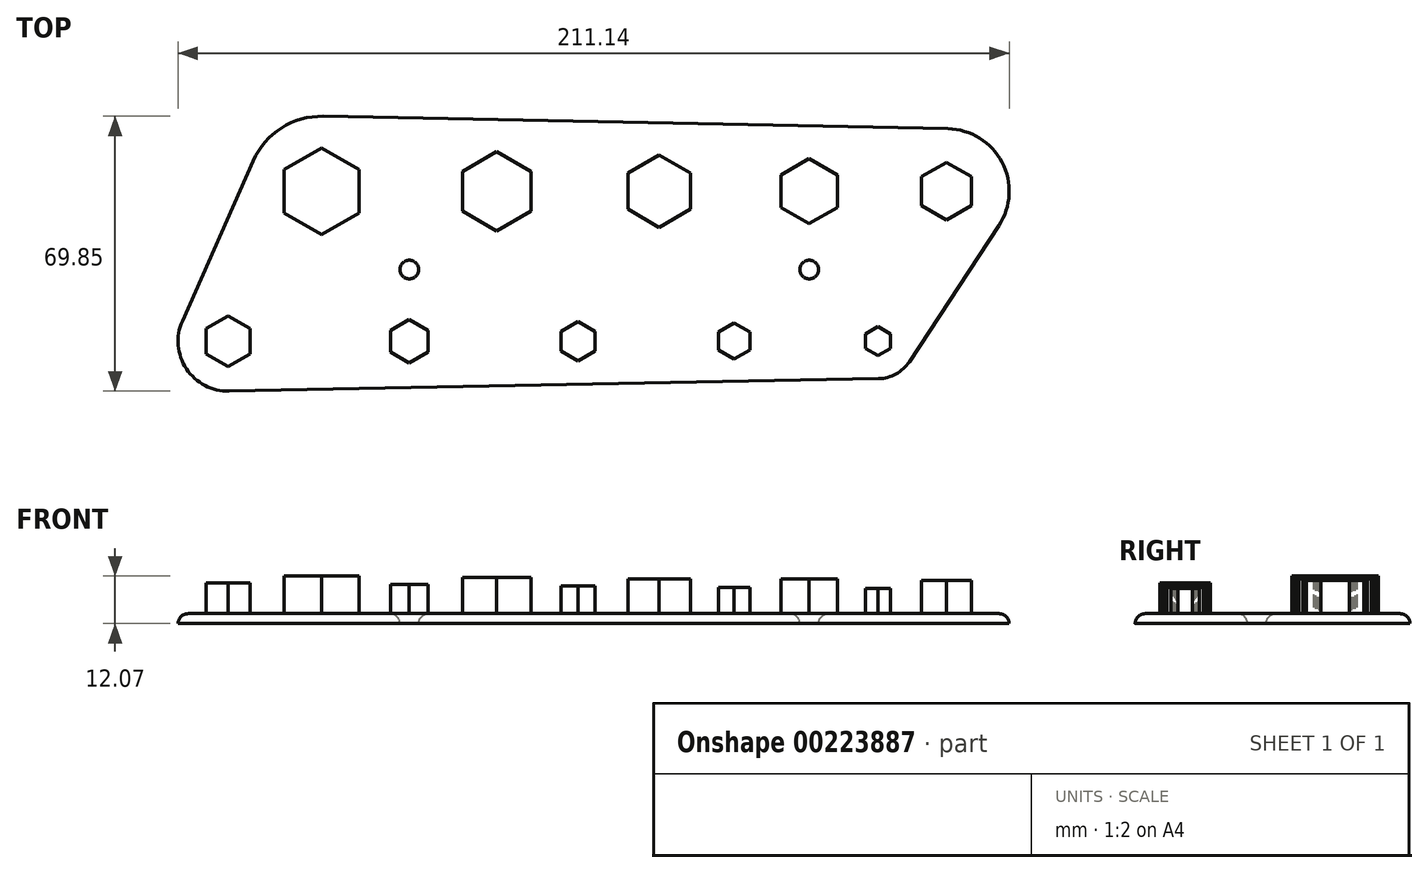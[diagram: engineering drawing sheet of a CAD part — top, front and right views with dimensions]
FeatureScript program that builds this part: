
annotation { "Feature Type Name" : "Feature", "Feature Type Description" : "" }
export const myFeature = defineFeature(function(context is Context, id is Id, definition is map)
    precondition{}
    {
        {
            var Q0;
            Q0=qCreatedBy(makeId("Top.planeOp"),FACE);
            var sketch = newSketch(context, id + "F0", { "sketchPlane" : qUnion([Q0])});
            skLineSegment(sketch, "E0", {"start": v(0, 0) * mm, "end": v(44.45, 0) * mm});
            skLineSegment(sketch, "E1", {"start": v(85.73, 0) * mm, "end": v(123.83, 0) * mm});
            skLineSegment(sketch, "E2", {"start": v(85.73, 0) * mm, "end": v(44.45, 0) * mm});
            skLineSegment(sketch, "E3", {"start": v(123.83, 0) * mm, "end": v(158.75, 0) * mm});
            skLineSegment(sketch, "E4", {"start": v(22.23, 0) * mm, "end": v(22.23, -38.1) * mm});
            skLineSegment(sketch, "E5", {"start": v(65.09, 0) * mm, "end": v(65.09, -38.1) * mm});
            skLineSegment(sketch, "E6", {"start": v(104.78, -38.1) * mm, "end": v(104.78, 0) * mm});
            skLineSegment(sketch, "E7", {"start": v(141.29, 0) * mm, "end": v(141.29, -38.1) * mm});
            skLineSegment(sketch, "E8", {"start": v(-23.81, -38.1) * mm, "end": v(22.23, -38.1) * mm});
            skCircle(sketch, "E9.cCircle", {"center": v(0, 0) * mm, "radius": 9.53 * mm, "construction": true});
            skLineSegment(sketch, "E9.0", {"start": v(9.53, 5.5) * mm, "end": v(9.53, -5.5) * mm});
            skLineSegment(sketch, "E9.1", {"start": v(9.52, -5.5) * mm, "end": v(0, -11) * mm});
            skLineSegment(sketch, "E9.2", {"start": v(0, -11) * mm, "end": v(-9.53, -5.5) * mm});
            skLineSegment(sketch, "E9.3", {"start": v(-9.53, -5.5) * mm, "end": v(-9.53, 5.5) * mm});
            skLineSegment(sketch, "E9.4", {"start": v(-9.53, 5.5) * mm, "end": v(0, 11) * mm});
            skLineSegment(sketch, "E9.5", {"start": v(0, 11) * mm, "end": v(9.53, 5.5) * mm});
            skPoint(sketch, "E9.0.midPoint", {"position": v(9.53, 0) * mm});
            skCircle(sketch, "E10.cCircle", {"center": v(44.45, 0) * mm, "radius": 8.73 * mm, "construction": true});
            skLineSegment(sketch, "E10.0", {"start": v(53.18, 5.04) * mm, "end": v(53.18, -5.04) * mm});
            skLineSegment(sketch, "E10.1", {"start": v(53.18, -5.04) * mm, "end": v(44.45, -10.08) * mm});
            skLineSegment(sketch, "E10.2", {"start": v(44.45, -10.08) * mm, "end": v(35.72, -5.04) * mm});
            skLineSegment(sketch, "E10.3", {"start": v(35.72, -5.04) * mm, "end": v(35.72, 5.04) * mm});
            skLineSegment(sketch, "E10.4", {"start": v(35.72, 5.04) * mm, "end": v(44.45, 10.08) * mm});
            skLineSegment(sketch, "E10.5", {"start": v(44.45, 10.08) * mm, "end": v(53.18, 5.04) * mm});
            skPoint(sketch, "E10.0.midPoint", {"position": v(53.18, 0) * mm});
            skCircle(sketch, "E11.cCircle", {"center": v(85.72, 0) * mm, "radius": 7.94 * mm, "construction": true});
            skLineSegment(sketch, "E11.0", {"start": v(93.66, 4.58) * mm, "end": v(93.66, -4.58) * mm});
            skLineSegment(sketch, "E11.1", {"start": v(93.66, -4.58) * mm, "end": v(85.73, -9.17) * mm});
            skLineSegment(sketch, "E11.2", {"start": v(85.72, -9.17) * mm, "end": v(77.79, -4.58) * mm});
            skLineSegment(sketch, "E11.3", {"start": v(77.79, -4.58) * mm, "end": v(77.79, 4.58) * mm});
            skLineSegment(sketch, "E11.4", {"start": v(77.79, 4.58) * mm, "end": v(85.72, 9.17) * mm});
            skLineSegment(sketch, "E11.5", {"start": v(85.72, 9.17) * mm, "end": v(93.66, 4.58) * mm});
            skPoint(sketch, "E11.0.midPoint", {"position": v(93.66, 0) * mm});
            skCircle(sketch, "E12.cCircle", {"center": v(123.83, 0) * mm, "radius": 7.14 * mm, "construction": true});
            skLineSegment(sketch, "E12.0", {"start": v(130.97, 4.12) * mm, "end": v(130.97, -4.12) * mm});
            skLineSegment(sketch, "E12.1", {"start": v(130.97, -4.12) * mm, "end": v(123.83, -8.25) * mm});
            skLineSegment(sketch, "E12.2", {"start": v(123.83, -8.25) * mm, "end": v(116.68, -4.12) * mm});
            skLineSegment(sketch, "E12.3", {"start": v(116.68, -4.12) * mm, "end": v(116.68, 4.12) * mm});
            skLineSegment(sketch, "E12.4", {"start": v(116.68, 4.12) * mm, "end": v(123.83, 8.25) * mm});
            skLineSegment(sketch, "E12.5", {"start": v(123.83, 8.25) * mm, "end": v(130.97, 4.12) * mm});
            skPoint(sketch, "E12.0.midPoint", {"position": v(130.97, 0) * mm});
            skCircle(sketch, "E13.cCircle", {"center": v(158.75, 0) * mm, "radius": 6.35 * mm, "construction": true});
            skLineSegment(sketch, "E13.0", {"start": v(152.4, -3.67) * mm, "end": v(152.4, 3.67) * mm});
            skLineSegment(sketch, "E13.1", {"start": v(152.4, 3.67) * mm, "end": v(158.75, 7.33) * mm});
            skLineSegment(sketch, "E13.2", {"start": v(158.75, 7.33) * mm, "end": v(165.1, 3.67) * mm});
            skLineSegment(sketch, "E13.3", {"start": v(165.1, 3.67) * mm, "end": v(165.1, -3.67) * mm});
            skLineSegment(sketch, "E13.4", {"start": v(165.1, -3.67) * mm, "end": v(158.75, -7.33) * mm});
            skLineSegment(sketch, "E13.5", {"start": v(158.75, -7.33) * mm, "end": v(152.4, -3.67) * mm});
            skPoint(sketch, "E13.0.midPoint", {"position": v(152.4, 0) * mm});
            skCircle(sketch, "E14.cCircle", {"center": v(-23.81, -38.1) * mm, "radius": 5.56 * mm, "construction": true});
            skLineSegment(sketch, "E14.0", {"start": v(-18.26, -34.9) * mm, "end": v(-18.26, -41.3) * mm});
            skLineSegment(sketch, "E14.1", {"start": v(-18.26, -41.3) * mm, "end": v(-23.81, -44.52) * mm});
            skLineSegment(sketch, "E14.2", {"start": v(-23.81, -44.52) * mm, "end": v(-29.37, -41.3) * mm});
            skLineSegment(sketch, "E14.3", {"start": v(-29.37, -41.3) * mm, "end": v(-29.37, -34.9) * mm});
            skLineSegment(sketch, "E14.4", {"start": v(-29.37, -34.9) * mm, "end": v(-23.81, -31.68) * mm});
            skLineSegment(sketch, "E14.5", {"start": v(-23.81, -31.68) * mm, "end": v(-18.26, -34.9) * mm});
            skPoint(sketch, "E14.0.midPoint", {"position": v(-18.26, -38.1) * mm});
            skCircle(sketch, "E15.cCircle", {"center": v(22.23, -38.1) * mm, "radius": 4.76 * mm, "construction": true});
            skLineSegment(sketch, "E15.0", {"start": v(26.99, -35.35) * mm, "end": v(26.99, -40.85) * mm});
            skLineSegment(sketch, "E15.1", {"start": v(26.99, -40.85) * mm, "end": v(22.23, -43.6) * mm});
            skLineSegment(sketch, "E15.2", {"start": v(22.23, -43.6) * mm, "end": v(17.46, -40.85) * mm});
            skLineSegment(sketch, "E15.3", {"start": v(17.46, -40.85) * mm, "end": v(17.46, -35.35) * mm});
            skLineSegment(sketch, "E15.4", {"start": v(17.46, -35.35) * mm, "end": v(22.23, -32.6) * mm});
            skLineSegment(sketch, "E15.5", {"start": v(22.23, -32.6) * mm, "end": v(26.99, -35.35) * mm});
            skPoint(sketch, "E15.0.midPoint", {"position": v(26.99, -38.1) * mm});
            skCircle(sketch, "E16.cCircle", {"center": v(65.09, -38.1) * mm, "radius": 4.37 * mm, "construction": true});
            skLineSegment(sketch, "E16.0", {"start": v(69.45, -35.58) * mm, "end": v(69.45, -40.62) * mm});
            skLineSegment(sketch, "E16.1", {"start": v(69.45, -40.62) * mm, "end": v(65.09, -43.14) * mm});
            skLineSegment(sketch, "E16.2", {"start": v(65.09, -43.14) * mm, "end": v(60.72, -40.62) * mm});
            skLineSegment(sketch, "E16.3", {"start": v(60.72, -40.62) * mm, "end": v(60.72, -35.58) * mm});
            skLineSegment(sketch, "E16.4", {"start": v(60.72, -35.58) * mm, "end": v(65.09, -33.06) * mm});
            skLineSegment(sketch, "E16.5", {"start": v(65.09, -33.06) * mm, "end": v(69.45, -35.58) * mm});
            skPoint(sketch, "E16.0.midPoint", {"position": v(69.45, -38.1) * mm});
            skCircle(sketch, "E17.cCircle", {"center": v(104.78, -38.1) * mm, "radius": 3.97 * mm, "construction": true});
            skLineSegment(sketch, "E17.0", {"start": v(108.74, -35.8) * mm, "end": v(108.74, -40.4) * mm});
            skLineSegment(sketch, "E17.1", {"start": v(108.74, -40.4) * mm, "end": v(104.78, -42.68) * mm});
            skLineSegment(sketch, "E17.2", {"start": v(104.78, -42.68) * mm, "end": v(100.8, -40.4) * mm});
            skLineSegment(sketch, "E17.3", {"start": v(100.8, -40.4) * mm, "end": v(100.8, -35.8) * mm});
            skLineSegment(sketch, "E17.4", {"start": v(100.8, -35.8) * mm, "end": v(104.78, -33.52) * mm});
            skLineSegment(sketch, "E17.5", {"start": v(104.78, -33.52) * mm, "end": v(108.74, -35.8) * mm});
            skPoint(sketch, "E17.0.midPoint", {"position": v(108.74, -38.1) * mm});
            skCircle(sketch, "E18.cCircle", {"center": v(141.29, -38.1) * mm, "radius": 3.18 * mm, "construction": true});
            skLineSegment(sketch, "E18.0", {"start": v(144.46, -36.27) * mm, "end": v(144.46, -39.93) * mm});
            skLineSegment(sketch, "E18.1", {"start": v(144.46, -39.93) * mm, "end": v(141.29, -41.77) * mm});
            skLineSegment(sketch, "E18.2", {"start": v(141.29, -41.77) * mm, "end": v(138.11, -39.93) * mm});
            skLineSegment(sketch, "E18.3", {"start": v(138.11, -39.93) * mm, "end": v(138.11, -36.27) * mm});
            skLineSegment(sketch, "E18.4", {"start": v(138.11, -36.27) * mm, "end": v(141.29, -34.43) * mm});
            skLineSegment(sketch, "E18.5", {"start": v(141.29, -34.43) * mm, "end": v(144.46, -36.27) * mm});
            skPoint(sketch, "E18.0.midPoint", {"position": v(144.46, -38.1) * mm});
            skSolve(sketch);
        }
        {
            var Q0;
            Q0 = qSketchRegion(id + "F0", true);
            extrude(context, id + "F1", {"entities" : qUnion([Q0]), "depth" : 6.35 * mm});
        }
        {
            var Q0;
            Q0=makeQuery(id+"F1.opExtrude","CAP_FACE",FACE,{"disambiguationData":[OSD([sQuery(id+"F0.wireOp",EDGE,"E9.0"),sQuery(id+"F0.wireOp",EDGE,"E9.1"),sQuery(id+"F0.wireOp",EDGE,"E9.2"),sQuery(id+"F0.wireOp",EDGE,"E9.3"),sQuery(id+"F0.wireOp",EDGE,"E9.4"),sQuery(id+"F0.wireOp",EDGE,"E9.5")])],"isStart":false});
            extrude(context, id + "F2", {"entities" : qUnion([Q0]), "operationType" : NewBodyOperationType.ADD, "depth" : 3.17 * mm});
        }
        {
            var Q0;
            Q0=makeQuery(id+"F1.opExtrude","CAP_FACE",FACE,{"disambiguationData":[OSD([sQuery(id+"F0.wireOp",EDGE,"E10.0"),sQuery(id+"F0.wireOp",EDGE,"E10.1"),sQuery(id+"F0.wireOp",EDGE,"E10.2"),sQuery(id+"F0.wireOp",EDGE,"E10.3"),sQuery(id+"F0.wireOp",EDGE,"E10.4"),sQuery(id+"F0.wireOp",EDGE,"E10.5")])],"isStart":false});
            extrude(context, id + "F3", {"entities" : qUnion([Q0]), "operationType" : NewBodyOperationType.ADD, "depth" : 2.82 * mm});
        }
        {
            var Q0;
            Q0=makeQuery(id+"F1.opExtrude","CAP_FACE",FACE,{"disambiguationData":[OSD([sQuery(id+"F0.wireOp",EDGE,"E11.0"),sQuery(id+"F0.wireOp",EDGE,"E11.1"),sQuery(id+"F0.wireOp",EDGE,"E11.2"),sQuery(id+"F0.wireOp",EDGE,"E11.3"),sQuery(id+"F0.wireOp",EDGE,"E11.4"),sQuery(id+"F0.wireOp",EDGE,"E11.5")])],"isStart":false});
            extrude(context, id + "F4", {"entities" : qUnion([Q0]), "operationType" : NewBodyOperationType.ADD, "depth" : 2.47 * mm});
        }
        {
            var Q0;
            Q0=makeQuery(id+"F1.opExtrude","CAP_FACE",FACE,{"disambiguationData":[OSD([sQuery(id+"F0.wireOp",EDGE,"E12.0"),sQuery(id+"F0.wireOp",EDGE,"E12.1"),sQuery(id+"F0.wireOp",EDGE,"E12.2"),sQuery(id+"F0.wireOp",EDGE,"E12.3"),sQuery(id+"F0.wireOp",EDGE,"E12.4"),sQuery(id+"F0.wireOp",EDGE,"E12.5")])],"isStart":false});
            extrude(context, id + "F5", {"entities" : qUnion([Q0]), "operationType" : NewBodyOperationType.ADD, "depth" : 2.47 * mm});
        }
        {
            var Q0;
            Q0=makeQuery(id+"F1.opExtrude","CAP_FACE",FACE,{"disambiguationData":[OSD([sQuery(id+"F0.wireOp",EDGE,"E13.0"),sQuery(id+"F0.wireOp",EDGE,"E13.1"),sQuery(id+"F0.wireOp",EDGE,"E13.2"),sQuery(id+"F0.wireOp",EDGE,"E13.3"),sQuery(id+"F0.wireOp",EDGE,"E13.4"),sQuery(id+"F0.wireOp",EDGE,"E13.5")])],"isStart":false});
            extrude(context, id + "F6", {"entities" : qUnion([Q0]), "operationType" : NewBodyOperationType.ADD, "depth" : 2.12 * mm});
        }
        {
            var Q0;
            Q0=makeQuery(id+"F1.opExtrude","CAP_FACE",FACE,{"disambiguationData":[OSD([sQuery(id+"F0.wireOp",EDGE,"E14.0"),sQuery(id+"F0.wireOp",EDGE,"E14.1"),sQuery(id+"F0.wireOp",EDGE,"E14.2"),sQuery(id+"F0.wireOp",EDGE,"E14.3"),sQuery(id+"F0.wireOp",EDGE,"E14.4"),sQuery(id+"F0.wireOp",EDGE,"E14.5")])],"isStart":false});
            extrude(context, id + "F7", {"entities" : qUnion([Q0]), "operationType" : NewBodyOperationType.ADD, "depth" : 1.41 * mm});
        }
        {
            var Q0;
            Q0=makeQuery(id+"F1.opExtrude","CAP_FACE",FACE,{"disambiguationData":[OSD([sQuery(id+"F0.wireOp",EDGE,"E15.0"),sQuery(id+"F0.wireOp",EDGE,"E15.1"),sQuery(id+"F0.wireOp",EDGE,"E15.2"),sQuery(id+"F0.wireOp",EDGE,"E15.3"),sQuery(id+"F0.wireOp",EDGE,"E15.4"),sQuery(id+"F0.wireOp",EDGE,"E15.5")])],"isStart":false});
            extrude(context, id + "F8", {"entities" : qUnion([Q0]), "operationType" : NewBodyOperationType.ADD, "depth" : 1.06 * mm});
        }
        {
            var Q0;
            Q0=makeQuery(id+"F1.opExtrude","CAP_FACE",FACE,{"disambiguationData":[OSD([sQuery(id+"F0.wireOp",EDGE,"E17.0"),sQuery(id+"F0.wireOp",EDGE,"E17.1"),sQuery(id+"F0.wireOp",EDGE,"E17.2"),sQuery(id+"F0.wireOp",EDGE,"E17.3"),sQuery(id+"F0.wireOp",EDGE,"E17.4"),sQuery(id+"F0.wireOp",EDGE,"E17.5")])],"isStart":false});
            extrude(context, id + "F9", {"entities" : qUnion([Q0]), "operationType" : NewBodyOperationType.ADD, "depth" : 0.35 * mm});
        }
        {
            var Q0;
            Q0=makeQuery(id+"F1.opExtrude","CAP_FACE",FACE,{"disambiguationData":[OSD([sQuery(id+"F0.wireOp",EDGE,"E16.0"),sQuery(id+"F0.wireOp",EDGE,"E16.1"),sQuery(id+"F0.wireOp",EDGE,"E16.2"),sQuery(id+"F0.wireOp",EDGE,"E16.3"),sQuery(id+"F0.wireOp",EDGE,"E16.4"),sQuery(id+"F0.wireOp",EDGE,"E16.5")])],"isStart":false});
            extrude(context, id + "F10", {"entities" : qUnion([Q0]), "operationType" : NewBodyOperationType.ADD, "depth" : 0.7 * mm});
        }
        {
            var Q0;
            Q0=makeQuery(id+"F1.opExtrude","CAP_FACE",FACE,{"disambiguationData":[OSD([sQuery(id+"F0.wireOp",EDGE,"E9.0"),sQuery(id+"F0.wireOp",EDGE,"E9.1"),sQuery(id+"F0.wireOp",EDGE,"E9.2"),sQuery(id+"F0.wireOp",EDGE,"E9.3"),sQuery(id+"F0.wireOp",EDGE,"E9.4"),sQuery(id+"F0.wireOp",EDGE,"E9.5")])],"isStart":true});
            var sketch = newSketch(context, id + "F11", { "sketchPlane" : qUnion([Q0])});
            skArc(sketch, "E19", {"start": v(-17.42, -7.71) * mm, "mid": v(3.94, -18.64) * mm, "end": v(19.05, 0) * mm});
            skArc(sketch, "E20", {"start": v(142.88, 0) * mm, "mid": v(163.3, -15.2) * mm, "end": v(172.01, 8.72) * mm});
            skArc(sketch, "E21", {"start": v(-11.11, 38.1) * mm, "mid": v(-26.44, 50.53) * mm, "end": v(-35.43, 32.96) * mm});
            skArc(sketch, "E22", {"start": v(149.25, 43.33) * mm, "mid": v(138.56, 47.22) * mm, "end": v(131.76, 38.1) * mm});
            skLineSegment(sketch, "E23", {"start": v(-23.81, 38.1) * mm, "end": v(141.29, 38.1) * mm});
            skLineSegment(sketch, "E24", {"start": v(0, 0) * mm, "end": v(158.75, 0) * mm});
            skLineSegment(sketch, "E25", {"start": v(-35.43, 32.96) * mm, "end": v(-17.42, -7.71) * mm});
            skLineSegment(sketch, "E26", {"start": v(-23.57, 50.8) * mm, "end": v(141.29, 47.63) * mm});
            skLineSegment(sketch, "E27", {"start": v(149.25, 43.33) * mm, "end": v(172.01, 8.72) * mm});
            skLineSegment(sketch, "E28", {"start": v(0.38, -19.05) * mm, "end": v(159.07, -15.87) * mm});
            skLineSegment(sketch, "E29", {"start": v(-23.57, 50.8) * mm, "end": v(141.47, 47.62) * mm});
            skSolve(sketch);
        }
        {
            var Q0;
            {var subQ0=sQuery(id+"F11.wireOp",EDGE,"E23");var subQ1=sQuery(id+"F11.wireOp",EDGE,"E21");var subQ2=makeQuery(id+"F11.imprint","INTERSECT",VERTEX,{"derivedFrom":[subQ1,subQ0]});Q0=makeQuery(id+"F11.imprint","IMPRINT",FACE,{"disambiguationData":[TD([[makeQuery(id+"F11.imprint","IMPRINT",EDGE,{"disambiguationData":[TD([[subQ2,-1.0]])],"derivedFrom":subQ1}),-1.0]])]});}
            var Q1;
            {var subQ11=sQuery(id+"F11.wireOp",EDGE,"E25");Q1=makeQuery(id+"F11.imprint","IMPRINT",FACE,{"disambiguationData":[TD([[makeQuery(id+"F11.imprint","IMPRINT",EDGE,{"derivedFrom":subQ11}),1.0]])]});}
            var Q2;
            {var subQ3=sQuery(id+"F11.wireOp",EDGE,"E28");Q2=makeQuery(id+"F11.imprint","IMPRINT",FACE,{"disambiguationData":[TD([[makeQuery(id+"F11.imprint","IMPRINT",EDGE,{"derivedFrom":subQ3}),1.0]])]});}
            extrude(context, id + "F12", {"entities" : qUnion([Q0, Q1, Q2]), "depth" : 2.54 * mm});
        }
        {
            var Q0;
            Q0=makeQuery(id+"F12.opExtrude","CAP_FACE",FACE,{"disambiguationData":[OSD([sQuery(id+"F0.wireOp",EDGE,"E9.0"),sQuery(id+"F0.wireOp",EDGE,"E9.1"),sQuery(id+"F0.wireOp",EDGE,"E9.2"),sQuery(id+"F0.wireOp",EDGE,"E9.3"),sQuery(id+"F0.wireOp",EDGE,"E9.4"),sQuery(id+"F0.wireOp",EDGE,"E9.5"),sQuery(id+"F11.wireOp",EDGE,"E19"),sQuery(id+"F11.wireOp",EDGE,"E20"),sQuery(id+"F11.wireOp",EDGE,"E21"),sQuery(id+"F11.wireOp",EDGE,"E22"),sQuery(id+"F11.wireOp",EDGE,"E25"),sQuery(id+"F11.wireOp",EDGE,"E27"),sQuery(id+"F11.wireOp",EDGE,"E28"),sQuery(id+"F11.wireOp",EDGE,"E29")])],"isStart":false});
            var sketch = newSketch(context, id + "F13", { "sketchPlane" : qUnion([Q0])});
            skCircle(sketch, "E30", {"center": v(22.23, 19.9) * mm, "radius": 2.38 * mm});
            skCircle(sketch, "E31", {"center": v(123.83, 19.9) * mm, "radius": 2.38 * mm});
            skSolve(sketch);
        }
        {
            var Q0;
            Q0=makeQuery(id+"F13.imprint","IMPRINT",FACE,{"disambiguationData":[TD([[makeQuery(id+"F13.imprint","IMPRINT",EDGE,{"derivedFrom":sQuery(id+"F13.wireOp",EDGE,"E30")}),1.0]])]});
            var Q1;
            Q1=makeQuery(id+"F13.imprint","IMPRINT",FACE,{"disambiguationData":[TD([[makeQuery(id+"F13.imprint","IMPRINT",EDGE,{"derivedFrom":sQuery(id+"F13.wireOp",EDGE,"E31")}),1.0]])]});
            extrude(context, id + "F14", {"entities" : qUnion([Q0, Q1]), "operationType" : NewBodyOperationType.REMOVE, "oppositeDirection" : true, "depth" : 25.4 * mm});
        }
        {
            var Q0;
            Q0=makeQuery(id+"F14.boolean.opBoolean","INTERSECT",EDGE,{"derivedFrom":[makeQuery(id+"F12.opExtrude","CAP_FACE",FACE,{"disambiguationData":[OSD([sQuery(id+"F0.wireOp",EDGE,"E9.0"),sQuery(id+"F0.wireOp",EDGE,"E9.1"),sQuery(id+"F0.wireOp",EDGE,"E9.2"),sQuery(id+"F0.wireOp",EDGE,"E9.3"),sQuery(id+"F0.wireOp",EDGE,"E9.4"),sQuery(id+"F0.wireOp",EDGE,"E9.5"),sQuery(id+"F11.wireOp",EDGE,"E19"),sQuery(id+"F11.wireOp",EDGE,"E20"),sQuery(id+"F11.wireOp",EDGE,"E21"),sQuery(id+"F11.wireOp",EDGE,"E22"),sQuery(id+"F11.wireOp",EDGE,"E25"),sQuery(id+"F11.wireOp",EDGE,"E27"),sQuery(id+"F11.wireOp",EDGE,"E28"),sQuery(id+"F11.wireOp",EDGE,"E29")])],"isStart":true}),makeQuery(id+"F14.opExtrude","SWEPT_FACE",FACE,{"disambiguationData":[OSD([sQuery(id+"F13.wireOp",EDGE,"E30")])]})]});
            fillet(context, id + "F15", {"entities" : qUnion([Q0]), "radius" : 2.54 * mm, "tangentPropagation" : true, "allowEdgeOverflow" : false});
        }
        {
            var Q0;
            Q0=makeQuery(id+"F12.opExtrude","CAP_EDGE",EDGE,{"disambiguationData":[OSD([sQuery(id+"F11.wireOp",EDGE,"E29")])],"isStart":true});
            var Q1;
            Q1=makeQuery(id+"F14.boolean.opBoolean","INTERSECT",EDGE,{"derivedFrom":[makeQuery(id+"F12.opExtrude","CAP_FACE",FACE,{"disambiguationData":[OSD([sQuery(id+"F0.wireOp",EDGE,"E9.0"),sQuery(id+"F0.wireOp",EDGE,"E9.1"),sQuery(id+"F0.wireOp",EDGE,"E9.2"),sQuery(id+"F0.wireOp",EDGE,"E9.3"),sQuery(id+"F0.wireOp",EDGE,"E9.4"),sQuery(id+"F0.wireOp",EDGE,"E9.5"),sQuery(id+"F11.wireOp",EDGE,"E19"),sQuery(id+"F11.wireOp",EDGE,"E20"),sQuery(id+"F11.wireOp",EDGE,"E21"),sQuery(id+"F11.wireOp",EDGE,"E22"),sQuery(id+"F11.wireOp",EDGE,"E25"),sQuery(id+"F11.wireOp",EDGE,"E27"),sQuery(id+"F11.wireOp",EDGE,"E28"),sQuery(id+"F11.wireOp",EDGE,"E29")])],"isStart":true}),makeQuery(id+"F14.opExtrude","SWEPT_FACE",FACE,{"disambiguationData":[OSD([sQuery(id+"F13.wireOp",EDGE,"E31")])]})]});
            fillet(context, id + "F16", {"entities" : qUnion([Q0, Q1]), "radius" : 2.54 * mm, "tangentPropagation" : true, "allowEdgeOverflow" : false});
        }
        {
            var Q0;
            Q0=makeQuery(id+"F1.opExtrude","SWEPT_BODY",BODY,{"disambiguationData":[OSD([sQuery(id+"F0.wireOp",EDGE,"E9.0"),sQuery(id+"F0.wireOp",EDGE,"E9.1"),sQuery(id+"F0.wireOp",EDGE,"E9.2"),sQuery(id+"F0.wireOp",EDGE,"E9.3"),sQuery(id+"F0.wireOp",EDGE,"E9.4"),sQuery(id+"F0.wireOp",EDGE,"E9.5")])]});
            var Q1;
            Q1=makeQuery(id+"F1.opExtrude","SWEPT_BODY",BODY,{"disambiguationData":[OSD([sQuery(id+"F0.wireOp",EDGE,"E10.0"),sQuery(id+"F0.wireOp",EDGE,"E10.1"),sQuery(id+"F0.wireOp",EDGE,"E10.2"),sQuery(id+"F0.wireOp",EDGE,"E10.3"),sQuery(id+"F0.wireOp",EDGE,"E10.4"),sQuery(id+"F0.wireOp",EDGE,"E10.5")])]});
            var Q2;
            Q2=makeQuery(id+"F1.opExtrude","SWEPT_BODY",BODY,{"disambiguationData":[OSD([sQuery(id+"F0.wireOp",EDGE,"E11.0"),sQuery(id+"F0.wireOp",EDGE,"E11.1"),sQuery(id+"F0.wireOp",EDGE,"E11.2"),sQuery(id+"F0.wireOp",EDGE,"E11.3"),sQuery(id+"F0.wireOp",EDGE,"E11.4"),sQuery(id+"F0.wireOp",EDGE,"E11.5")])]});
            var Q3;
            Q3=makeQuery(id+"F1.opExtrude","SWEPT_BODY",BODY,{"disambiguationData":[OSD([sQuery(id+"F0.wireOp",EDGE,"E12.0"),sQuery(id+"F0.wireOp",EDGE,"E12.1"),sQuery(id+"F0.wireOp",EDGE,"E12.2"),sQuery(id+"F0.wireOp",EDGE,"E12.3"),sQuery(id+"F0.wireOp",EDGE,"E12.4"),sQuery(id+"F0.wireOp",EDGE,"E12.5")])]});
            var Q4;
            Q4=makeQuery(id+"F1.opExtrude","SWEPT_BODY",BODY,{"disambiguationData":[OSD([sQuery(id+"F0.wireOp",EDGE,"E13.0"),sQuery(id+"F0.wireOp",EDGE,"E13.1"),sQuery(id+"F0.wireOp",EDGE,"E13.2"),sQuery(id+"F0.wireOp",EDGE,"E13.3"),sQuery(id+"F0.wireOp",EDGE,"E13.4"),sQuery(id+"F0.wireOp",EDGE,"E13.5")])]});
            var Q5;
            Q5=makeQuery(id+"F1.opExtrude","SWEPT_BODY",BODY,{"disambiguationData":[OSD([sQuery(id+"F0.wireOp",EDGE,"E14.0"),sQuery(id+"F0.wireOp",EDGE,"E14.1"),sQuery(id+"F0.wireOp",EDGE,"E14.2"),sQuery(id+"F0.wireOp",EDGE,"E14.3"),sQuery(id+"F0.wireOp",EDGE,"E14.4"),sQuery(id+"F0.wireOp",EDGE,"E14.5")])]});
            var Q6;
            Q6=makeQuery(id+"F1.opExtrude","SWEPT_BODY",BODY,{"disambiguationData":[OSD([sQuery(id+"F0.wireOp",EDGE,"E15.0"),sQuery(id+"F0.wireOp",EDGE,"E15.1"),sQuery(id+"F0.wireOp",EDGE,"E15.2"),sQuery(id+"F0.wireOp",EDGE,"E15.3"),sQuery(id+"F0.wireOp",EDGE,"E15.4"),sQuery(id+"F0.wireOp",EDGE,"E15.5")])]});
            var Q7;
            Q7=makeQuery(id+"F1.opExtrude","SWEPT_BODY",BODY,{"disambiguationData":[OSD([sQuery(id+"F0.wireOp",EDGE,"E16.0"),sQuery(id+"F0.wireOp",EDGE,"E16.1"),sQuery(id+"F0.wireOp",EDGE,"E16.2"),sQuery(id+"F0.wireOp",EDGE,"E16.3"),sQuery(id+"F0.wireOp",EDGE,"E16.4"),sQuery(id+"F0.wireOp",EDGE,"E16.5")])]});
            var Q8;
            Q8=makeQuery(id+"F1.opExtrude","SWEPT_BODY",BODY,{"disambiguationData":[OSD([sQuery(id+"F0.wireOp",EDGE,"E17.0"),sQuery(id+"F0.wireOp",EDGE,"E17.1"),sQuery(id+"F0.wireOp",EDGE,"E17.2"),sQuery(id+"F0.wireOp",EDGE,"E17.3"),sQuery(id+"F0.wireOp",EDGE,"E17.4"),sQuery(id+"F0.wireOp",EDGE,"E17.5")])]});
            var Q9;
            Q9=makeQuery(id+"F1.opExtrude","SWEPT_BODY",BODY,{"disambiguationData":[OSD([sQuery(id+"F0.wireOp",EDGE,"E18.0"),sQuery(id+"F0.wireOp",EDGE,"E18.1"),sQuery(id+"F0.wireOp",EDGE,"E18.2"),sQuery(id+"F0.wireOp",EDGE,"E18.3"),sQuery(id+"F0.wireOp",EDGE,"E18.4"),sQuery(id+"F0.wireOp",EDGE,"E18.5")])]});
            var Q10;
            Q10=makeQuery(id+"F12.opExtrude","SWEPT_BODY",BODY,{"disambiguationData":[OSD([sQuery(id+"F0.wireOp",EDGE,"E9.0"),sQuery(id+"F0.wireOp",EDGE,"E9.1"),sQuery(id+"F0.wireOp",EDGE,"E9.2"),sQuery(id+"F0.wireOp",EDGE,"E9.3"),sQuery(id+"F0.wireOp",EDGE,"E9.4"),sQuery(id+"F0.wireOp",EDGE,"E9.5"),sQuery(id+"F11.wireOp",EDGE,"E19"),sQuery(id+"F11.wireOp",EDGE,"E20"),sQuery(id+"F11.wireOp",EDGE,"E21"),sQuery(id+"F11.wireOp",EDGE,"E22"),sQuery(id+"F11.wireOp",EDGE,"E25"),sQuery(id+"F11.wireOp",EDGE,"E27"),sQuery(id+"F11.wireOp",EDGE,"E28"),sQuery(id+"F11.wireOp",EDGE,"E29")])]});
            booleanBodies(context, id + "F17", {"operationType" : BooleanOperationType.UNION, "tools" : qUnion([Q0, Q1, Q2, Q3, Q4, Q5, Q6, Q7, Q8, Q9, Q10])});
        }
        {
            var Q0;
            Q0=makeQuery(id+"F1.opExtrude","CAP_FACE",FACE,{"disambiguationData":[OSD([sQuery(id+"F0.wireOp",EDGE,"E9.0"),sQuery(id+"F0.wireOp",EDGE,"E9.1"),sQuery(id+"F0.wireOp",EDGE,"E9.2"),sQuery(id+"F0.wireOp",EDGE,"E9.3"),sQuery(id+"F0.wireOp",EDGE,"E9.4"),sQuery(id+"F0.wireOp",EDGE,"E9.5")])],"isStart":true});
            var Q1;
            Q1=makeQuery(id+"F12.opExtrude","CAP_FACE",FACE,{"disambiguationData":[OSD([sQuery(id+"F0.wireOp",EDGE,"E9.0"),sQuery(id+"F0.wireOp",EDGE,"E9.1"),sQuery(id+"F0.wireOp",EDGE,"E9.2"),sQuery(id+"F0.wireOp",EDGE,"E9.3"),sQuery(id+"F0.wireOp",EDGE,"E9.4"),sQuery(id+"F0.wireOp",EDGE,"E9.5"),sQuery(id+"F11.wireOp",EDGE,"E19"),sQuery(id+"F11.wireOp",EDGE,"E20"),sQuery(id+"F11.wireOp",EDGE,"E21"),sQuery(id+"F11.wireOp",EDGE,"E22"),sQuery(id+"F11.wireOp",EDGE,"E25"),sQuery(id+"F11.wireOp",EDGE,"E27"),sQuery(id+"F11.wireOp",EDGE,"E28"),sQuery(id+"F11.wireOp",EDGE,"E29")])],"isStart":false});
            extrude(context, id + "F18", {"entities" : qUnion([Q0]), "operationType" : NewBodyOperationType.ADD, "endBound" : BoundingType.UP_TO_SURFACE, "endBoundEntityFace" : qUnion([Q1]), "depth" : 25.4 * mm});
        }
    });
